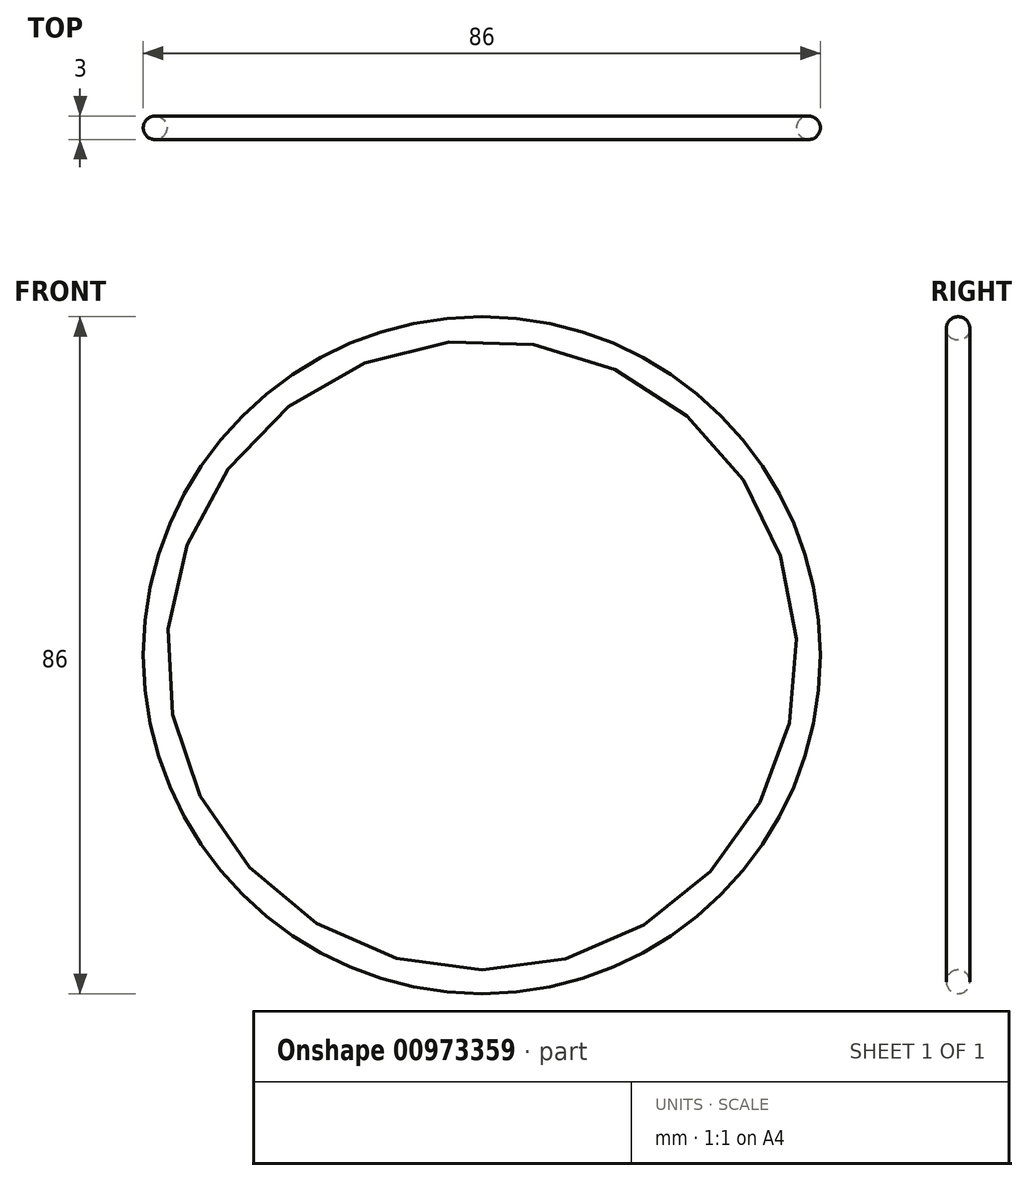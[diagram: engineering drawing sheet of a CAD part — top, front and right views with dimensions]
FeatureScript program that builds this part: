
annotation { "Feature Type Name" : "Feature", "Feature Type Description" : "" }
export const myFeature = defineFeature(function(context is Context, id is Id, definition is map)
    precondition{}
    {
        {
            var Q0;
            Q0=qCreatedBy(makeId("Top.planeOp"),FACE);
            var sketch = newSketch(context, id + "F0", { "sketchPlane" : qUnion([Q0])});
            skLineSegment(sketch, "E0", {"start": v(0, 0) * mm, "end": v(41.5, 0) * mm});
            skLineSegment(sketch, "E1", {"start": v(0, -1.72) * mm, "end": v(0, 1.84) * mm});
            skCircle(sketch, "E2", {"center": v(41.5, 0) * mm, "radius": 1.5 * mm});
            skPoint(sketch, "E3", {"position": v(40, 0) * mm});
            skSolve(sketch);
        }
        {
            var Q0;
            Q0=makeQuery(id+"F0.imprint","IMPRINT",FACE,{"disambiguationData":[TD([[makeQuery(id+"F0.imprint","IMPRINT",EDGE,{"derivedFrom":sQuery(id+"F0.wireOp",EDGE,"E2")}),1.0]])]});
            var Q1;
            Q1=sQuery(id+"F0.wireOp",EDGE,"E1");
            revolve(context, id + "F1", {"surfaceOperationType" : NewSurfaceOperationType.NEW, "entities" : qUnion([Q0]), "axis" : qUnion([Q1]), "revolveType" : RevolveType.FULL});
        }
    });
